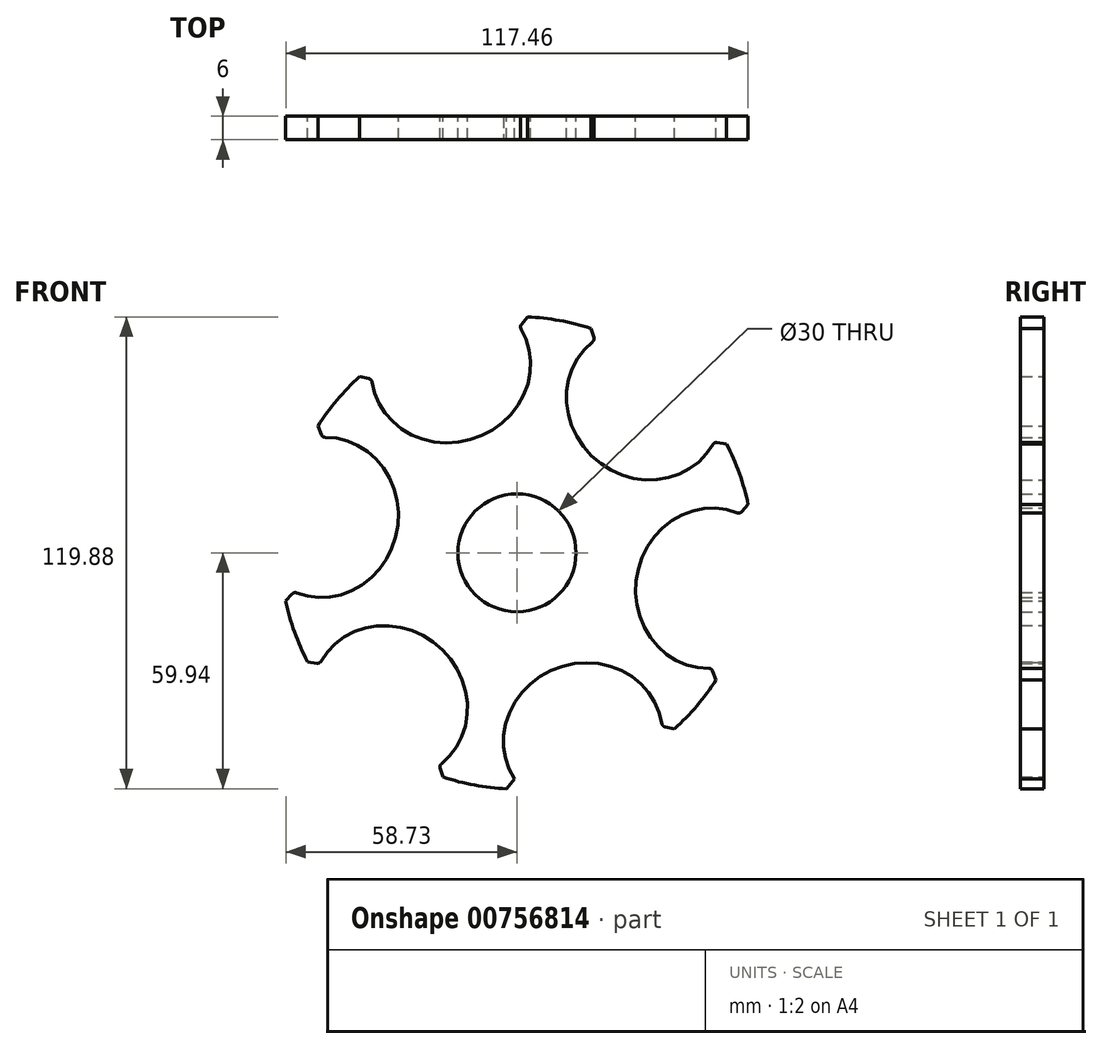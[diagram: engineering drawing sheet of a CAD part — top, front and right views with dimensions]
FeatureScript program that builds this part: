
annotation { "Feature Type Name" : "Feature", "Feature Type Description" : "" }
export const myFeature = defineFeature(function(context is Context, id is Id, definition is map)
    precondition{}
    {
        {
            var Q0;
            Q0=qCreatedBy(makeId("Front.planeOp"),FACE);
            var sketch = newSketch(context, id + "F0", { "sketchPlane" : qUnion([Q0])});
            skCircle(sketch, "E0", {"center": v(-25, 43.3) * mm, "radius": 11.5 * mm, "construction": true});
            skCircle(sketch, "E1", {"center": v(0, 0) * mm, "radius": 31 * mm, "construction": true});
            skCircle(sketch, "E2", {"center": v(0, 0) * mm, "radius": 50 * mm, "construction": true});
            skPoint(sketch, "E3", {"position": v(-10.41, 29.2) * mm});
            skEllipticalArc(sketch, "E4", {});
            skCircle(sketch, "E5", {"center": v(0, 0) * mm, "radius": 57.5 * mm, "construction": true});
            skArc(sketch, "E6", {"start": v(-39.98, 44.74) * mm, "mid": v(-45.71, 38.86) * mm, "end": v(-50.59, 32.27) * mm});
            skLineSegment(sketch, "E7", {"start": v(-36.91, 44.09) * mm, "end": v(-39.98, 44.74) * mm});
            skLineSegment(sketch, "E8.MirrorCS", {"start": v(0.69, 57.5) * mm, "end": v(2.65, 59.94) * mm});
            skLineSegment(sketch, "E9.1.0", {"start": v(-56.64, -9.93) * mm, "end": v(-58.73, -12.26) * mm});
            skEllipticalArc(sketch, "E9.1.1", {});
            skLineSegment(sketch, "E9.1.2", {"start": v(-49.45, 29.34) * mm, "end": v(-50.59, 32.27) * mm});
            skLineSegment(sketch, "E9.2.0", {"start": v(-19.72, -54.01) * mm, "end": v(-18.75, -57) * mm});
            skEllipticalArc(sketch, "E9.2.1", {});
            skLineSegment(sketch, "E9.2.2", {"start": v(-50.14, -28.15) * mm, "end": v(-53.24, -27.68) * mm});
            skLineSegment(sketch, "E9.3.0", {"start": v(36.91, -44.09) * mm, "end": v(39.98, -44.74) * mm});
            skEllipticalArc(sketch, "E9.3.1", {});
            skLineSegment(sketch, "E9.3.2", {"start": v(-0.69, -57.5) * mm, "end": v(-2.65, -59.94) * mm});
            skLineSegment(sketch, "E9.4.0", {"start": v(56.64, 9.93) * mm, "end": v(58.73, 12.26) * mm});
            skEllipticalArc(sketch, "E9.4.1", {});
            skLineSegment(sketch, "E9.4.2", {"start": v(49.45, -29.34) * mm, "end": v(50.59, -32.27) * mm});
            skLineSegment(sketch, "E9.5.0", {"start": v(19.72, 54.01) * mm, "end": v(18.75, 57) * mm});
            skEllipticalArc(sketch, "E9.5.1", {});
            skLineSegment(sketch, "E9.5.2", {"start": v(50.14, 28.15) * mm, "end": v(53.24, 27.68) * mm});
            skArc(sketch, "E10.trimOffspring", {"start": v(18.75, 57) * mm, "mid": v(10.8, 59.02) * mm, "end": v(2.65, 59.94) * mm});
            skArc(sketch, "E11.trimOffspring", {"start": v(58.73, 12.26) * mm, "mid": v(56.51, 20.16) * mm, "end": v(53.24, 27.68) * mm});
            skArc(sketch, "E12.trimOffspring", {"start": v(39.98, -44.74) * mm, "mid": v(45.71, -38.86) * mm, "end": v(50.59, -32.27) * mm});
            skArc(sketch, "E13.trimOffspring", {"start": v(-18.75, -57) * mm, "mid": v(-10.8, -59.02) * mm, "end": v(-2.65, -59.94) * mm});
            skArc(sketch, "E14.trimOffspring", {"start": v(-58.73, -12.26) * mm, "mid": v(-56.51, -20.16) * mm, "end": v(-53.24, -27.68) * mm});
            skCircle(sketch, "E15", {"center": v(0, 0) * mm, "radius": 15 * mm});
            const initialGuessF0  = {"E4": [-0.01679647611187887, 0.04709435624597786, 0.9418871249196011, 0.3359295222374594, 0.0204, 0.019, 2.9335459830375497, 0.2080466705522644], "E9.1.1": [-0.04918314693983061, 0.009001003116043361, 0.18002006232099219, 0.9836629387965912, 0.0204, 0.019, 2.933545983037551, 0.2080466705522651], "E9.2.1": [-0.032386670827951755, -0.0380933531299345, -0.76186706259861, 0.6477334165591316, 0.0204, 0.019, 2.933545983037549, 0.20804667055226378], "E9.3.1": [0.01679647611187886, -0.04709435624597786, -0.941887124919601, -0.33592952223745953, 0.0204, 0.019, 2.933545983037549, 0.20804667055226417], "E9.4.1": [0.04918314693983062, -0.009001003116043356, -0.1800200623209922, -0.9836629387965912, 0.0204, 0.019, 2.9335459830375505, 0.20804667055226397], "E9.5.1": [0.03238667082795174, 0.038093353129934504, 0.7618670625986101, -0.6477334165591319, 0.0204, 0.019, 2.93354598303755, 0.2080466705522645]};
            skSetInitialGuess(sketch, initialGuessF0);
            skSolve(sketch);
        }
        {
            var Q0;
            Q0 = qSketchRegion(id + "F0", true);
            extrude(context, id + "F1", {"entities" : qUnion([Q0]), "depth" : 6 * mm, "offsetDistance" : 25 * mm});
        }
        {
            var Q0;
            Q0=makeQuery(id+"F1.opExtrude","SWEPT_EDGE",EDGE,{"disambiguationData":[OSD([sQuery(id+"F0.wireOp",EDGE,"E4"),sQuery(id+"F0.wireOp",EDGE,"E7")])]});
            var Q1;
            Q1=makeQuery(id+"F1.opExtrude","SWEPT_EDGE",EDGE,{"disambiguationData":[OSD([sQuery(id+"F0.wireOp",EDGE,"E9.5.0"),sQuery(id+"F0.wireOp",EDGE,"E9.5.1")])]});
            var Q2;
            Q2=makeQuery(id+"F1.opExtrude","SWEPT_EDGE",EDGE,{"disambiguationData":[OSD([sQuery(id+"F0.wireOp",EDGE,"E9.4.0"),sQuery(id+"F0.wireOp",EDGE,"E9.4.1")])]});
            var Q3;
            Q3=makeQuery(id+"F1.opExtrude","SWEPT_EDGE",EDGE,{"disambiguationData":[OSD([sQuery(id+"F0.wireOp",EDGE,"E9.3.0"),sQuery(id+"F0.wireOp",EDGE,"E9.3.1")])]});
            var Q4;
            Q4=makeQuery(id+"F1.opExtrude","SWEPT_EDGE",EDGE,{"disambiguationData":[OSD([sQuery(id+"F0.wireOp",EDGE,"E9.2.0"),sQuery(id+"F0.wireOp",EDGE,"E9.2.1")])]});
            var Q5;
            Q5=makeQuery(id+"F1.opExtrude","SWEPT_EDGE",EDGE,{"disambiguationData":[OSD([sQuery(id+"F0.wireOp",EDGE,"E9.1.0"),sQuery(id+"F0.wireOp",EDGE,"E9.1.1")])]});
            var Q6;
            Q6=makeQuery(id+"F1.opExtrude","SWEPT_EDGE",EDGE,{"disambiguationData":[OSD([sQuery(id+"F0.wireOp",EDGE,"E9.1.1"),sQuery(id+"F0.wireOp",EDGE,"E9.1.2")])]});
            var Q7;
            Q7=makeQuery(id+"F1.opExtrude","SWEPT_EDGE",EDGE,{"disambiguationData":[OSD([sQuery(id+"F0.wireOp",EDGE,"E9.2.1"),sQuery(id+"F0.wireOp",EDGE,"E9.2.2")])]});
            var Q8;
            Q8=makeQuery(id+"F1.opExtrude","SWEPT_EDGE",EDGE,{"disambiguationData":[OSD([sQuery(id+"F0.wireOp",EDGE,"E9.4.1"),sQuery(id+"F0.wireOp",EDGE,"E9.4.2")])]});
            var Q9;
            Q9=makeQuery(id+"F1.opExtrude","SWEPT_EDGE",EDGE,{"disambiguationData":[OSD([sQuery(id+"F0.wireOp",EDGE,"E9.5.1"),sQuery(id+"F0.wireOp",EDGE,"E9.5.2")])]});
            var Q10;
            Q10=makeQuery(id+"F1.opExtrude","SWEPT_EDGE",EDGE,{"disambiguationData":[OSD([sQuery(id+"F0.wireOp",EDGE,"E4"),sQuery(id+"F0.wireOp",EDGE,"E8.MirrorCS")])]});
            fillet(context, id + "F2", {"entities" : qUnion([Q0, Q1, Q2, Q3, Q4, Q5, Q6, Q7, Q8, Q9, Q10]), "radius" : 1 * mm, "tangentPropagation" : true, "allowEdgeOverflow" : false});
        }
    });
